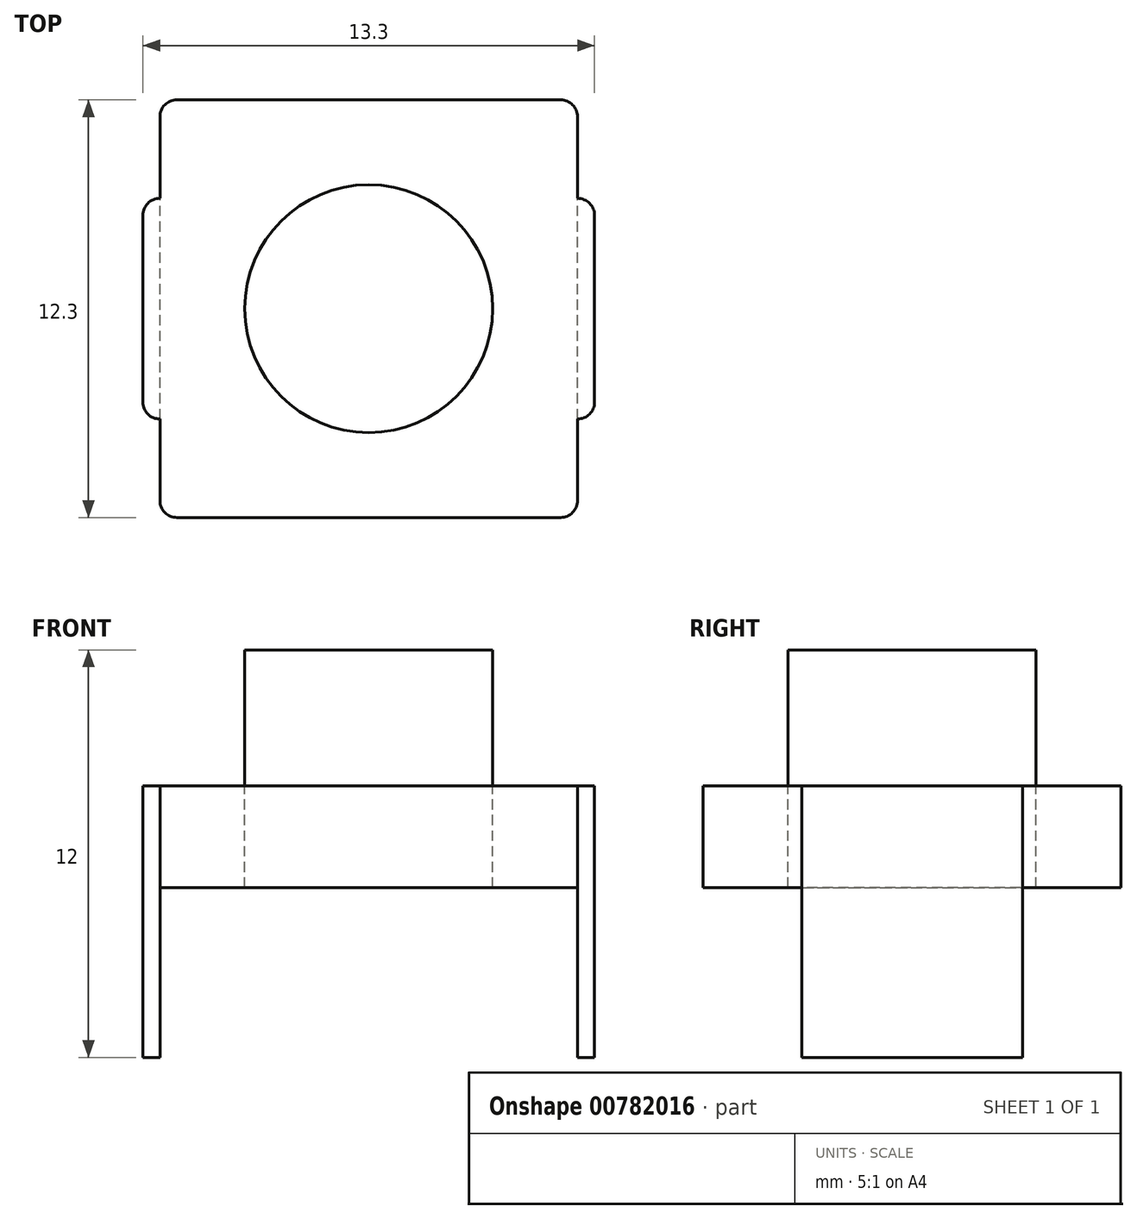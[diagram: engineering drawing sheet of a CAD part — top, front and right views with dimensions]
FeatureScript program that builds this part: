
annotation { "Feature Type Name" : "Feature", "Feature Type Description" : "" }
export const myFeature = defineFeature(function(context is Context, id is Id, definition is map)
    precondition{}
    {
        {
            var Q0;
            Q0=qCreatedBy(makeId("Top.planeOp"),FACE);
            var sketch = newSketch(context, id + "F0", { "sketchPlane" : qUnion([Q0])});
            skCircle(sketch, "E0", {"center": v(0, 0) * mm, "radius": 3.65 * mm});
            skLineSegment(sketch, "E1.bottom", {"start": v(-5.65, -6.15) * mm, "end": v(5.65, -6.15) * mm});
            skLineSegment(sketch, "E1.top", {"start": v(-5.65, 6.15) * mm, "end": v(5.65, 6.15) * mm});
            skLineSegment(sketch, "E1.left", {"start": v(-6.15, -5.65) * mm, "end": v(-6.15, 5.65) * mm});
            skLineSegment(sketch, "E1.right", {"start": v(6.15, -5.65) * mm, "end": v(6.15, 5.65) * mm});
            skPoint(sketch, "E2.start.orphan", {"position": v(0, -9.4) * mm});
            skLineSegment(sketch, "E3", {"start": v(0, 0) * mm, "end": v(6.15, 0) * mm, "construction": true});
            skLineSegment(sketch, "E4", {"start": v(0, 0) * mm, "end": v(-6.15, 0) * mm, "construction": true});
            skPoint(sketch, "E4.endSnap0", {"position": v(-6.15, 0) * mm});
            skLineSegment(sketch, "E5", {"start": v(0, 6.15) * mm, "end": v(0, -6.15) * mm, "construction": true});
            skLineSegment(sketch, "E6", {"start": v(-6.15, 3.25) * mm, "end": v(-6.15, 3.25) * mm});
            skLineSegment(sketch, "E7", {"start": v(-6.65, 0) * mm, "end": v(-6.65, -2.75) * mm});
            skLineSegment(sketch, "E8", {"start": v(-6.15, -3.25) * mm, "end": v(-6.15, -3.25) * mm});
            skLineSegment(sketch, "E9", {"start": v(-6.15, 0) * mm, "end": v(-6.65, 0) * mm, "construction": true});
            skLineSegment(sketch, "E10", {"start": v(-6.65, 2.75) * mm, "end": v(-6.65, 0) * mm});
            skLineSegment(sketch, "E11.MirrorCS", {"start": v(6.15, 3.25) * mm, "end": v(6.15, 3.25) * mm});
            skLineSegment(sketch, "E12.MirrorCS", {"start": v(6.65, 2.75) * mm, "end": v(6.65, 0) * mm});
            skLineSegment(sketch, "E13.MirrorCS", {"start": v(6.65, 0) * mm, "end": v(6.65, -2.75) * mm});
            skLineSegment(sketch, "E14.MirrorCS", {"start": v(6.15, -3.25) * mm, "end": v(6.15, -3.25) * mm});
            skArc(sketch, "E15.filletArc", {"start": v(-6.15, -5.65) * mm, "mid": v(-6, -6) * mm, "end": v(-5.65, -6.15) * mm});
            skPoint(sketch, "E16.visualSharp", {"position": v(-6.65, 3.25) * mm});
            skArc(sketch, "E16.filletArc", {"start": v(-6.15, 3.25) * mm, "mid": v(-6.5, 3.1) * mm, "end": v(-6.65, 2.75) * mm});
            skPoint(sketch, "E17.visualSharp", {"position": v(-6.15, 6.15) * mm});
            skArc(sketch, "E17.filletArc", {"start": v(-5.65, 6.15) * mm, "mid": v(-6, 6) * mm, "end": v(-6.15, 5.65) * mm});
            skPoint(sketch, "E18.visualSharp", {"position": v(6.15, 6.15) * mm});
            skArc(sketch, "E18.filletArc", {"start": v(6.15, 5.65) * mm, "mid": v(6, 6) * mm, "end": v(5.65, 6.15) * mm});
            skPoint(sketch, "E19.visualSharp", {"position": v(6.15, -6.15) * mm});
            skArc(sketch, "E19.filletArc", {"start": v(5.65, -6.15) * mm, "mid": v(6, -6) * mm, "end": v(6.15, -5.65) * mm});
            skPoint(sketch, "E20.visualSharp", {"position": v(6.65, 3.25) * mm});
            skArc(sketch, "E20.filletArc", {"start": v(6.65, 2.75) * mm, "mid": v(6.5, 3.1) * mm, "end": v(6.15, 3.25) * mm});
            skPoint(sketch, "E21.visualSharp", {"position": v(6.65, -3.25) * mm});
            skArc(sketch, "E21.filletArc", {"start": v(6.15, -3.25) * mm, "mid": v(6.5, -3.1) * mm, "end": v(6.65, -2.75) * mm});
            skPoint(sketch, "E22.visualSharp", {"position": v(-6.65, -3.25) * mm});
            skArc(sketch, "E22.filletArc", {"start": v(-6.65, -2.75) * mm, "mid": v(-6.5, -3.1) * mm, "end": v(-6.15, -3.25) * mm});
            skSolve(sketch);
        }
        {
            var Q0;
            Q0=makeQuery(id+"F0.imprint","IMPRINT",FACE,{"disambiguationData":[TD([[makeQuery(id+"F0.imprint","IMPRINT",EDGE,{"derivedFrom":sQuery(id+"F0.wireOp",EDGE,"E0")}),1.0]])]});
            extrude(context, id + "F1", {"entities" : qUnion([Q0]), "oppositeDirection" : true, "depth" : 7 * mm, "offsetDistance" : 25 * mm});
        }
        {
            var Q0;
            Q0=makeQuery(id+"F0.imprint","IMPRINT",FACE,{"disambiguationData":[TD([[makeQuery(id+"F0.imprint","IMPRINT",EDGE,{"derivedFrom":sQuery(id+"F0.wireOp",EDGE,"E0")}),-1.0]])]});
            extrude(context, id + "F2", {"entities" : qUnion([Q0]), "oppositeDirection" : true, "depth" : 7 * mm, "offsetDistance" : 25 * mm, "hasSecondDirection" : true, "secondDirectionOppositeDirection" : true, "secondDirectionDepth" : 4 * mm});
        }
        {
            var Q0;
            Q0=makeQuery(id+"F0.imprint","IMPRINT",FACE,{"disambiguationData":[TD([[makeQuery(id+"F0.imprint","IMPRINT",EDGE,{"derivedFrom":sQuery(id+"F0.wireOp",EDGE,"E7")}),1.0]])]});
            var Q1;
            Q1=makeQuery(id+"F0.imprint","IMPRINT",FACE,{"disambiguationData":[TD([[makeQuery(id+"F0.imprint","IMPRINT",EDGE,{"derivedFrom":sQuery(id+"F0.wireOp",EDGE,"E12.MirrorCS")}),-1.0]])]});
            extrude(context, id + "F3", {"entities" : qUnion([Q0, Q1]), "operationType" : NewBodyOperationType.ADD, "oppositeDirection" : true, "depth" : 12 * mm, "offsetDistance" : 25 * mm, "hasSecondDirection" : true, "secondDirectionOppositeDirection" : true, "secondDirectionDepth" : 4 * mm});
        }
    });
